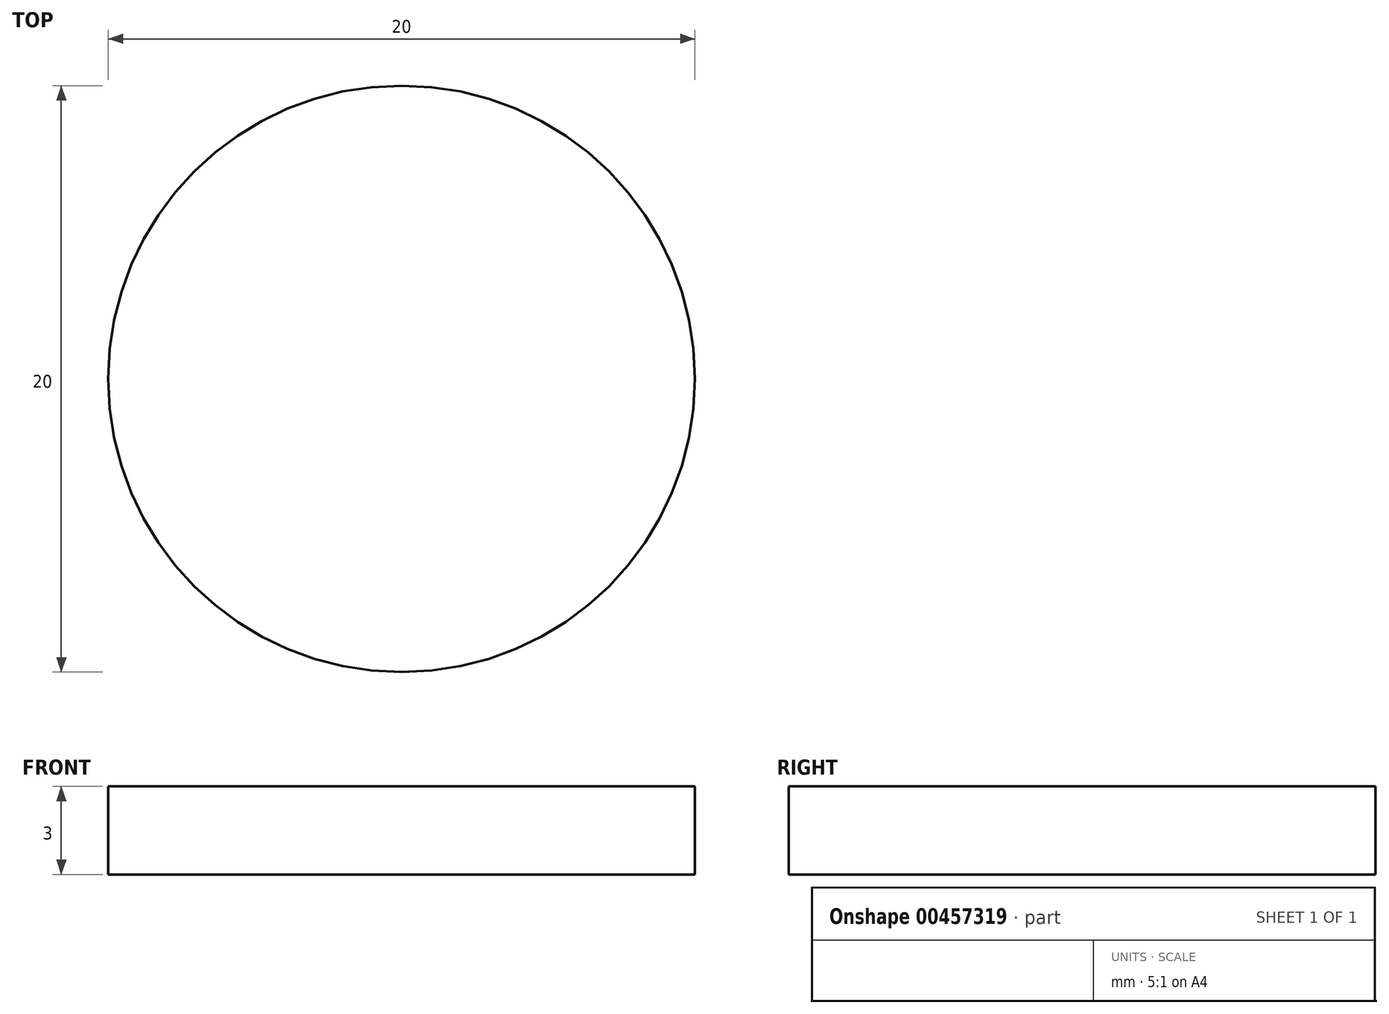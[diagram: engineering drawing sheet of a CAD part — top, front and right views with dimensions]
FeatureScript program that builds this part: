
annotation { "Feature Type Name" : "Feature", "Feature Type Description" : "" }
export const myFeature = defineFeature(function(context is Context, id is Id, definition is map)
    precondition{}
    {
        {
            var Q0;
            Q0=qCreatedBy(makeId("Top.planeOp"),FACE);
            var sketch = newSketch(context, id + "F0", { "sketchPlane" : qUnion([Q0])});
            skCircle(sketch, "E0", {"center": v(0, 0) * mm, "radius": 10 * mm});
            skSolve(sketch);
        }
        {
            var Q0;
            Q0=makeQuery(id+"F0.imprint","IMPRINT",FACE,{"disambiguationData":[TD([[makeQuery(id+"F0.imprint","IMPRINT",EDGE,{"derivedFrom":sQuery(id+"F0.wireOp",EDGE,"E0")}),1.0]])]});
            extrude(context, id + "F1", {"entities" : qUnion([Q0]), "depth" : 3 * mm});
        }
    });
